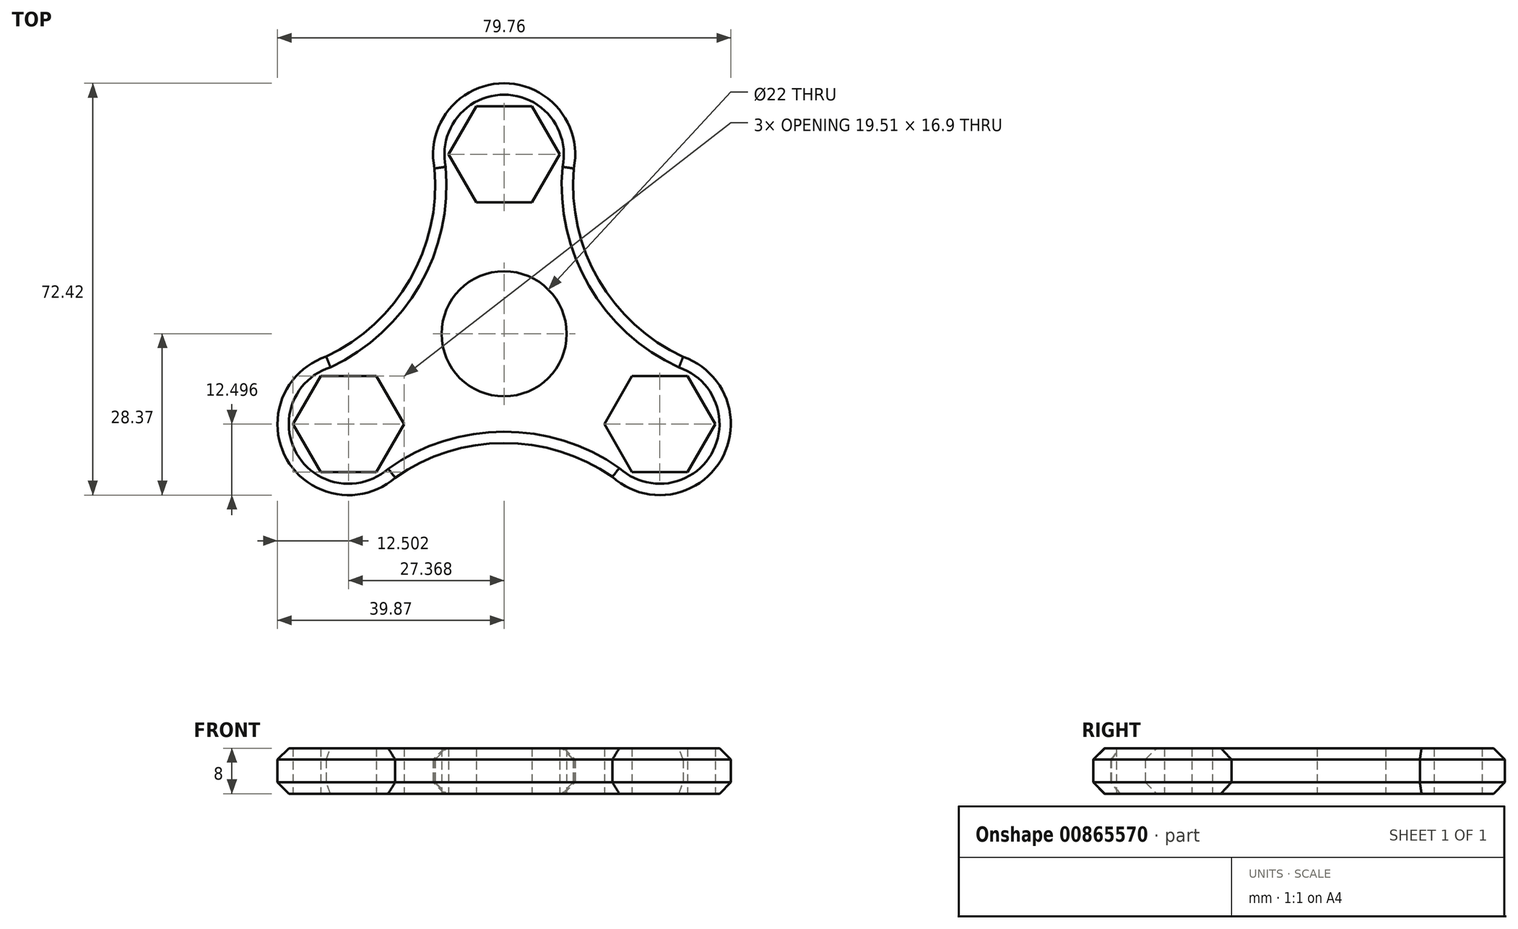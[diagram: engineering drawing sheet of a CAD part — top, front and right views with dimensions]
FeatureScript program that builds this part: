
annotation { "Feature Type Name" : "Feature", "Feature Type Description" : "" }
export const myFeature = defineFeature(function(context is Context, id is Id, definition is map)
    precondition{}
    {
        {
            var Q0;
            Q0=qCreatedBy(makeId("Top.planeOp"),FACE);
            var sketch = newSketch(context, id + "F0", { "sketchPlane" : qUnion([Q0])});
            skCircle(sketch, "E0", {"center": v(0, 0) * mm, "radius": 11 * mm});
            skCircle(sketch, "E1.cCircle", {"center": v(0, 31.55) * mm, "radius": 8.45 * mm, "construction": true});
            skLineSegment(sketch, "E1.0", {"start": v(4.88, 23.1) * mm, "end": v(-4.88, 23.1) * mm});
            skLineSegment(sketch, "E1.1", {"start": v(-4.88, 23.1) * mm, "end": v(-9.76, 31.55) * mm});
            skLineSegment(sketch, "E1.2", {"start": v(-9.76, 31.55) * mm, "end": v(-4.88, 40) * mm});
            skLineSegment(sketch, "E1.3", {"start": v(-4.88, 40) * mm, "end": v(4.88, 40) * mm});
            skLineSegment(sketch, "E1.4", {"start": v(4.88, 40) * mm, "end": v(9.76, 31.55) * mm});
            skLineSegment(sketch, "E1.5", {"start": v(9.76, 31.55) * mm, "end": v(4.88, 23.1) * mm});
            skPoint(sketch, "E1.0.midPoint", {"position": v(0, 23.1) * mm});
            skArc(sketch, "E2", {"start": v(12.25, 29.07) * mm, "mid": v(0, 44.05) * mm, "end": v(-12.25, 29.07) * mm});
            skCircle(sketch, "E3", {"center": v(0, 0) * mm, "radius": 31.55 * mm, "construction": true});
            skArc(sketch, "E4.2.0", {"start": v(-31.3, -4) * mm, "mid": v(-38.23, -22.06) * mm, "end": v(-19.16, -25.3) * mm});
            skLineSegment(sketch, "E4.2.1", {"start": v(-32.25, -24.32) * mm, "end": v(-37.13, -15.87) * mm});
            skLineSegment(sketch, "E4.2.2", {"start": v(-22.49, -24.32) * mm, "end": v(-32.25, -24.32) * mm});
            skLineSegment(sketch, "E4.2.3", {"start": v(-17.61, -15.87) * mm, "end": v(-22.49, -24.32) * mm});
            skLineSegment(sketch, "E4.2.4", {"start": v(-22.49, -7.42) * mm, "end": v(-17.61, -15.87) * mm});
            skLineSegment(sketch, "E4.2.5", {"start": v(-32.25, -7.42) * mm, "end": v(-22.49, -7.42) * mm});
            skLineSegment(sketch, "E4.2.6", {"start": v(-37.13, -15.87) * mm, "end": v(-32.25, -7.42) * mm});
            skPoint(sketch, "E4.center", {"position": v(0, -0.06) * mm});
            skArc(sketch, "E5.1.4.0", {"start": v(19.03, -25.16) * mm, "mid": v(38.15, -22.22) * mm, "end": v(31.49, -4.05) * mm});
            skLineSegment(sketch, "E5.2.4.0", {"start": v(37.14, -15.86) * mm, "end": v(32.27, -24.31) * mm});
            skLineSegment(sketch, "E5.5.4.0", {"start": v(32.27, -7.41) * mm, "end": v(37.14, -15.86) * mm});
            skLineSegment(sketch, "E5.8.4.0", {"start": v(22.5, -7.41) * mm, "end": v(32.27, -7.41) * mm});
            skLineSegment(sketch, "E5.11.4.0", {"start": v(17.63, -15.86) * mm, "end": v(22.5, -7.41) * mm});
            skLineSegment(sketch, "E5.14.4.0", {"start": v(22.5, -24.31) * mm, "end": v(17.63, -15.86) * mm});
            skLineSegment(sketch, "E5.17.4.0", {"start": v(32.27, -24.31) * mm, "end": v(22.5, -24.31) * mm});
            skLineSegment(sketch, "E6", {"start": v(-27.4, 15.83) * mm, "end": v(0, 0) * mm, "construction": true});
            skLineSegment(sketch, "E7", {"start": v(27.4, 15.82) * mm, "end": v(0, 0) * mm, "construction": true});
            skLineSegment(sketch, "E8", {"start": v(0, -0.06) * mm, "end": v(0, -31.71) * mm, "construction": true});
            skArc(sketch, "E9", {"start": v(-31.3, -4) * mm, "mid": v(-16.56, 9.53) * mm, "end": v(-12.25, 29.07) * mm});
            skPoint(sketch, "E9.first.point", {"position": v(-12.25, 29.07) * mm});
            skPoint(sketch, "E9.second.point", {"position": v(-16.55, 9.56) * mm});
            skPoint(sketch, "E9.third.point", {"position": v(-31.3, -4) * mm});
            skArc(sketch, "E10.1.0", {"start": v(19.03, -25.16) * mm, "mid": v(-0.08, -19.21) * mm, "end": v(-19.16, -25.3) * mm});
            skArc(sketch, "E10.2.0", {"start": v(12.25, 29.07) * mm, "mid": v(16.63, 9.47) * mm, "end": v(31.49, -4.05) * mm});
            skPoint(sketch, "E10.center", {"position": v(0.01, -0.06) * mm});
            skPoint(sketch, "E11.orphan", {"position": v(12.5, 31.17) * mm});
            skPoint(sketch, "E12.orphan", {"position": v(-12.5, 31.08) * mm});
            skPoint(sketch, "E13.orphan", {"position": v(33.24, -4.8) * mm});
            skPoint(sketch, "E14.orphan", {"position": v(20.81, -26.49) * mm});
            skPoint(sketch, "E15.orphan", {"position": v(-20.7, -26.46) * mm});
            skPoint(sketch, "E16.orphan", {"position": v(-33.28, -4.86) * mm});
            skSolve(sketch);
        }
        {
            var Q0;
            Q0 = qSketchRegion(id + "F0", true);
            extrude(context, id + "F1", {"entities" : qUnion([Q0]), "endBound" : BoundingType.SYMMETRIC, "depth" : 8 * mm, "offsetDistance" : 25 * mm});
        }
        {
            var Q0;
            Q0=makeQuery(id+"F1.opExtrude","CAP_EDGE",EDGE,{"disambiguationData":[OSD([sQuery(id+"F0.wireOp",EDGE,"E9")])],"isStart":false});
            var Q1;
            Q1=makeQuery(id+"F1.opExtrude","CAP_EDGE",EDGE,{"disambiguationData":[OSD([sQuery(id+"F0.wireOp",EDGE,"E2")])],"isStart":false});
            var Q2;
            Q2=makeQuery(id+"F1.opExtrude","CAP_EDGE",EDGE,{"disambiguationData":[OSD([sQuery(id+"F0.wireOp",EDGE,"E10.2.0")])],"isStart":false});
            var Q3;
            Q3=makeQuery(id+"F1.opExtrude","CAP_EDGE",EDGE,{"disambiguationData":[OSD([sQuery(id+"F0.wireOp",EDGE,"E5.1.4.0")])],"isStart":false});
            var Q4;
            Q4=makeQuery(id+"F1.opExtrude","CAP_EDGE",EDGE,{"disambiguationData":[OSD([sQuery(id+"F0.wireOp",EDGE,"E10.1.0")])],"isStart":false});
            var Q5;
            Q5=makeQuery(id+"F1.opExtrude","CAP_EDGE",EDGE,{"disambiguationData":[OSD([sQuery(id+"F0.wireOp",EDGE,"E4.2.0")])],"isStart":false});
            var Q6;
            Q6=makeQuery(id+"F1.opExtrude","CAP_EDGE",EDGE,{"disambiguationData":[OSD([sQuery(id+"F0.wireOp",EDGE,"E9")])],"isStart":true});
            var Q7;
            Q7=makeQuery(id+"F1.opExtrude","CAP_EDGE",EDGE,{"disambiguationData":[OSD([sQuery(id+"F0.wireOp",EDGE,"E2")])],"isStart":true});
            var Q8;
            Q8=makeQuery(id+"F1.opExtrude","CAP_EDGE",EDGE,{"disambiguationData":[OSD([sQuery(id+"F0.wireOp",EDGE,"E10.2.0")])],"isStart":true});
            var Q9;
            Q9=makeQuery(id+"F1.opExtrude","CAP_EDGE",EDGE,{"disambiguationData":[OSD([sQuery(id+"F0.wireOp",EDGE,"E5.1.4.0")])],"isStart":true});
            var Q10;
            Q10=makeQuery(id+"F1.opExtrude","CAP_EDGE",EDGE,{"disambiguationData":[OSD([sQuery(id+"F0.wireOp",EDGE,"E10.1.0")])],"isStart":true});
            var Q11;
            Q11=makeQuery(id+"F1.opExtrude","CAP_EDGE",EDGE,{"disambiguationData":[OSD([sQuery(id+"F0.wireOp",EDGE,"E4.2.0")])],"isStart":true});
            chamfer(context, id + "F2", {"entities" : qUnion([Q0, Q1, Q2, Q3, Q4, Q5, Q6, Q7, Q8, Q9, Q10, Q11]), "width" : 2 * mm, "tangentPropagation" : true});
        }
    });
